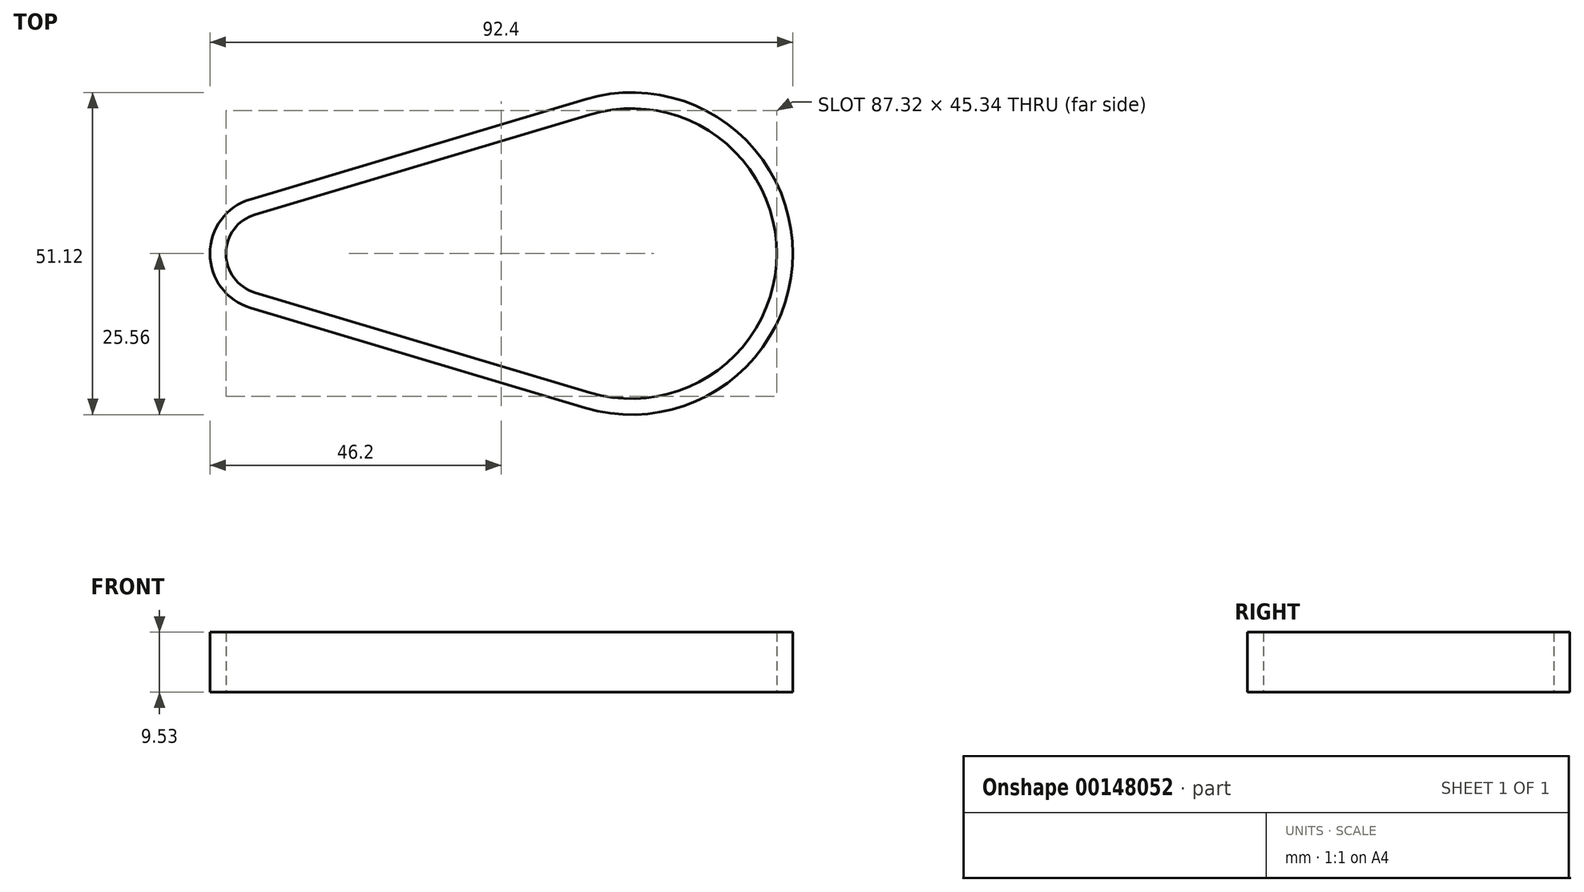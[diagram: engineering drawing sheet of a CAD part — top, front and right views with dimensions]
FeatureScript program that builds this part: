
annotation { "Feature Type Name" : "Feature", "Feature Type Description" : "" }
export const myFeature = defineFeature(function(context is Context, id is Id, definition is map)
    precondition{}
    {
        {
            var Q0;
            Q0=qCreatedBy(makeId("Top.planeOp"),FACE);
            var sketch = newSketch(context, id + "F0", { "sketchPlane" : qUnion([Q0])});
            skLineSegment(sketch, "E0", {"start": v(0, 0) * mm, "end": v(-57.85, 0) * mm, "construction": true});
            skArc(sketch, "E1", {"start": v(-6.6, -22.05) * mm, "mid": v(23.02, 0) * mm, "end": v(-6.6, 22.05) * mm});
            skArc(sketch, "E2", {"start": v(-59.7, 6.18) * mm, "mid": v(-64.3, 0) * mm, "end": v(-59.7, -6.18) * mm});
            skLineSegment(sketch, "E3", {"start": v(-59.7, 6.18) * mm, "end": v(-6.6, 22.05) * mm});
            skLineSegment(sketch, "E4", {"start": v(-59.7, -6.18) * mm, "end": v(-6.6, -22.05) * mm});
            skLineSegment(sketch, "E5", {"start": v(-59.7, 6.18) * mm, "end": v(-60.42, 8.61) * mm, "construction": true});
            skLineSegment(sketch, "E6", {"start": v(-59.7, -6.18) * mm, "end": v(-60.42, -8.61) * mm, "construction": true});
            skLineSegment(sketch, "E7", {"start": v(-60.42, 8.61) * mm, "end": v(-7.32, 24.49) * mm});
            skLineSegment(sketch, "E8", {"start": v(-60.42, -8.61) * mm, "end": v(-7.32, -24.49) * mm});
            skArc(sketch, "E9", {"start": v(-60.42, 8.61) * mm, "mid": v(-66.84, 0) * mm, "end": v(-60.42, -8.61) * mm});
            skArc(sketch, "E10", {"start": v(-7.32, -24.49) * mm, "mid": v(25.56, 0) * mm, "end": v(-7.32, 24.49) * mm});
            skSolve(sketch);
        }
        {
            var Q0;
            Q0=qSketchRegion(id+"F0",true);
            extrude(context, id + "F1", {"entities" : qUnion([Q0]), "depth" : 9.52 * mm});
        }
    });
